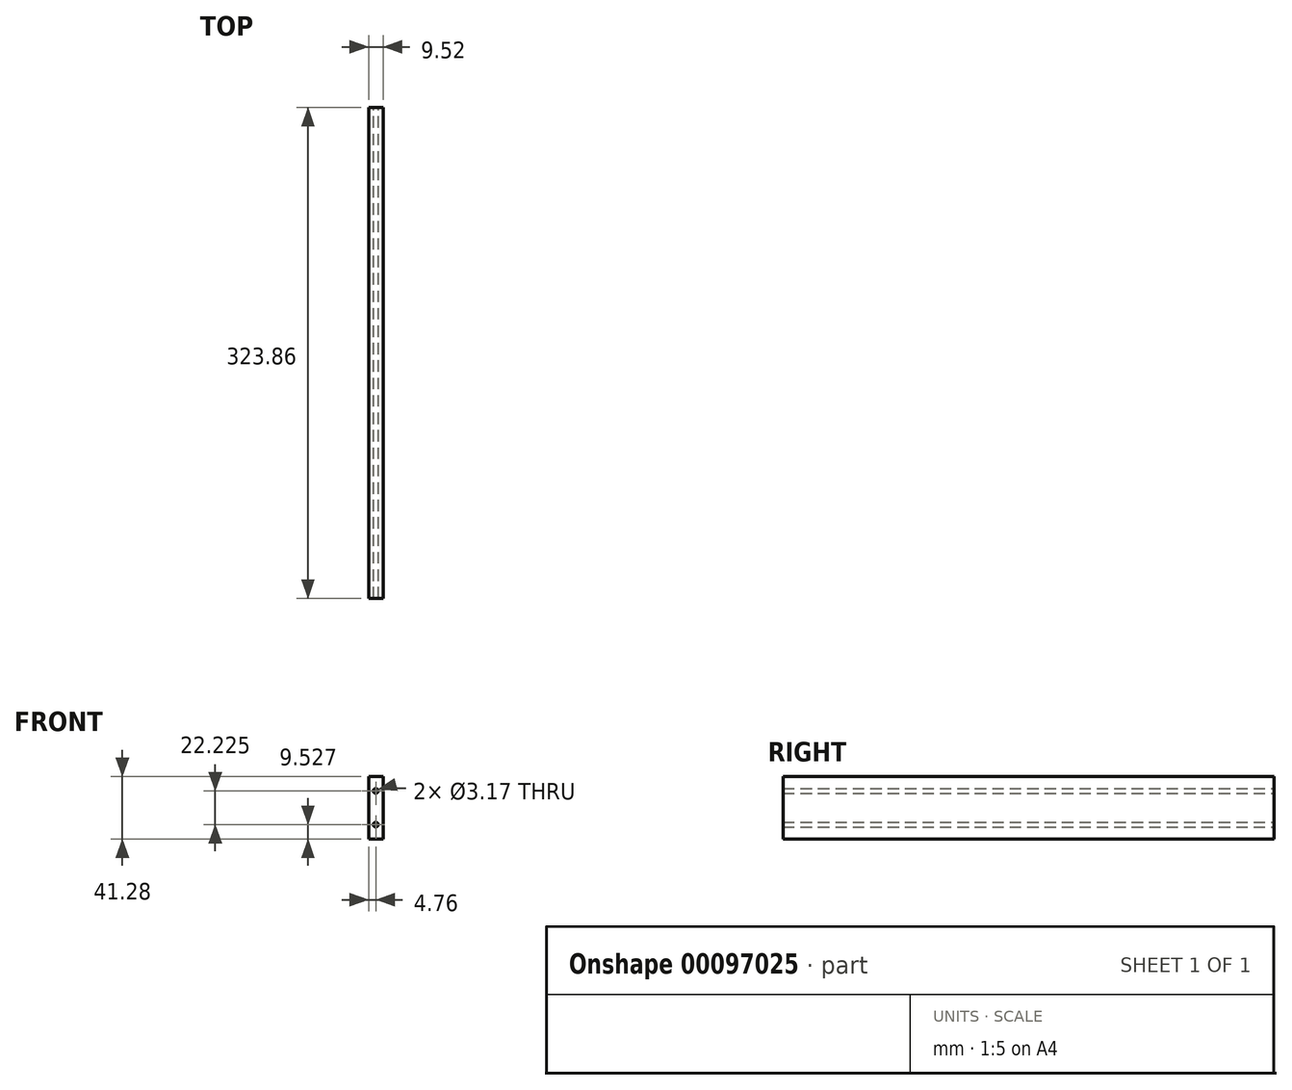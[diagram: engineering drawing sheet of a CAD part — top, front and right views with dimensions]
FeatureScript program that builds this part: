
annotation { "Feature Type Name" : "Feature", "Feature Type Description" : "" }
export const myFeature = defineFeature(function(context is Context, id is Id, definition is map)
    precondition{}
    {
        {
            var Q0;
            Q0=qCreatedBy(makeId("Front.planeOp"),FACE);
            var sketch = newSketch(context, id + "F0", { "sketchPlane" : qUnion([Q0])});
            skLineSegment(sketch, "E0.bottom", {"start": v(-4.76, 20.64) * mm, "end": v(4.76, 20.64) * mm});
            skLineSegment(sketch, "E0.top", {"start": v(-4.76, -20.64) * mm, "end": v(4.76, -20.64) * mm});
            skLineSegment(sketch, "E0.left", {"start": v(-4.76, 20.64) * mm, "end": v(-4.76, -20.64) * mm});
            skLineSegment(sketch, "E0.right", {"start": v(4.76, 20.64) * mm, "end": v(4.76, -20.64) * mm});
            skCircle(sketch, "E1", {"center": v(0, 11.11) * mm, "radius": 1.59 * mm});
            skCircle(sketch, "E2.MirrorC", {"center": v(0, -11.11) * mm, "radius": 1.59 * mm});
            skSolve(sketch);
        }
        {
            var Q0;
            Q0 = qSketchRegion(id + "F0", true);
            extrude(context, id + "F1", {"entities" : qUnion([Q0]), "endBound" : BoundingType.SYMMETRIC, "depth" : 323.85 * mm});
        }
    });
